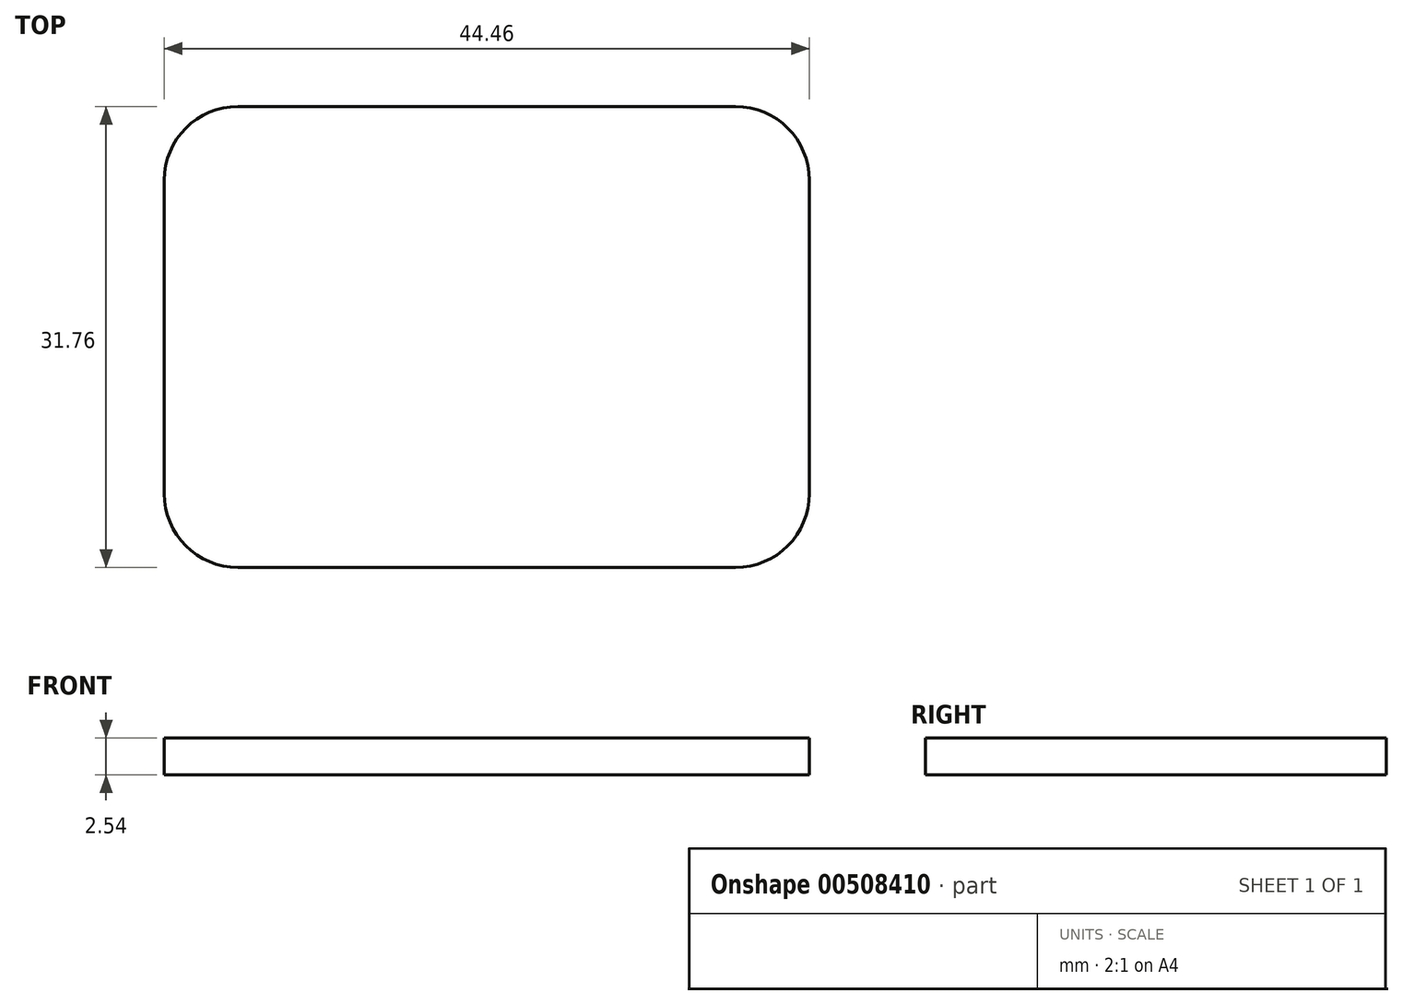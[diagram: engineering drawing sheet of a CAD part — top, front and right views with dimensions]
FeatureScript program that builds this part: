
annotation { "Feature Type Name" : "Feature", "Feature Type Description" : "" }
export const myFeature = defineFeature(function(context is Context, id is Id, definition is map)
    precondition{}
    {
        {
            var Q0;
            Q0=qCreatedBy(makeId("Front.planeOp"),FACE);
            var sketch = newSketch(context, id + "F0", { "sketchPlane" : qUnion([Q0])});
            skLineSegment(sketch, "E0.bottom", {"start": v(-22.23, 1.27) * mm, "end": v(22.22, 1.27) * mm});
            skLineSegment(sketch, "E0.top", {"start": v(-22.23, -1.27) * mm, "end": v(22.22, -1.27) * mm});
            skLineSegment(sketch, "E0.left", {"start": v(-22.23, 1.27) * mm, "end": v(-22.23, -1.27) * mm});
            skLineSegment(sketch, "E0.right", {"start": v(22.22, 1.27) * mm, "end": v(22.22, -1.27) * mm});
            skPoint(sketch, "E0.middle", {"position": v(0, 0) * mm});
            skSolve(sketch);
        }
        {
            var Q0;
            Q0=makeQuery(id+"F0.imprint","IMPRINT",FACE,{"disambiguationData":[TD([[makeQuery(id+"F0.imprint","IMPRINT",EDGE,{"derivedFrom":sQuery(id+"F0.wireOp",EDGE,"E0.bottom")}),-1.0]])]});
            extrude(context, id + "F1", {"entities" : qUnion([Q0]), "endBound" : BoundingType.SYMMETRIC, "depth" : 31.75 * mm});
        }
        {
            var Q0;
            Q0=makeQuery(id+"F1.opExtrude","CAP_EDGE",EDGE,{"disambiguationData":[OSD([sQuery(id+"F0.wireOp",EDGE,"E0.left")])],"isStart":false});
            var Q1;
            Q1=makeQuery(id+"F1.opExtrude","CAP_EDGE",EDGE,{"disambiguationData":[OSD([sQuery(id+"F0.wireOp",EDGE,"E0.right")])],"isStart":false});
            var Q2;
            Q2=makeQuery(id+"F1.opExtrude","CAP_EDGE",EDGE,{"disambiguationData":[OSD([sQuery(id+"F0.wireOp",EDGE,"E0.right")])],"isStart":true});
            var Q3;
            Q3=makeQuery(id+"F1.opExtrude","CAP_EDGE",EDGE,{"disambiguationData":[OSD([sQuery(id+"F0.wireOp",EDGE,"E0.left")])],"isStart":true});
            fillet(context, id + "F2", {"entities" : qUnion([Q0, Q1, Q2, Q3]), "radius" : 5.08 * mm, "tangentPropagation" : true, "allowEdgeOverflow" : false});
        }
    });
